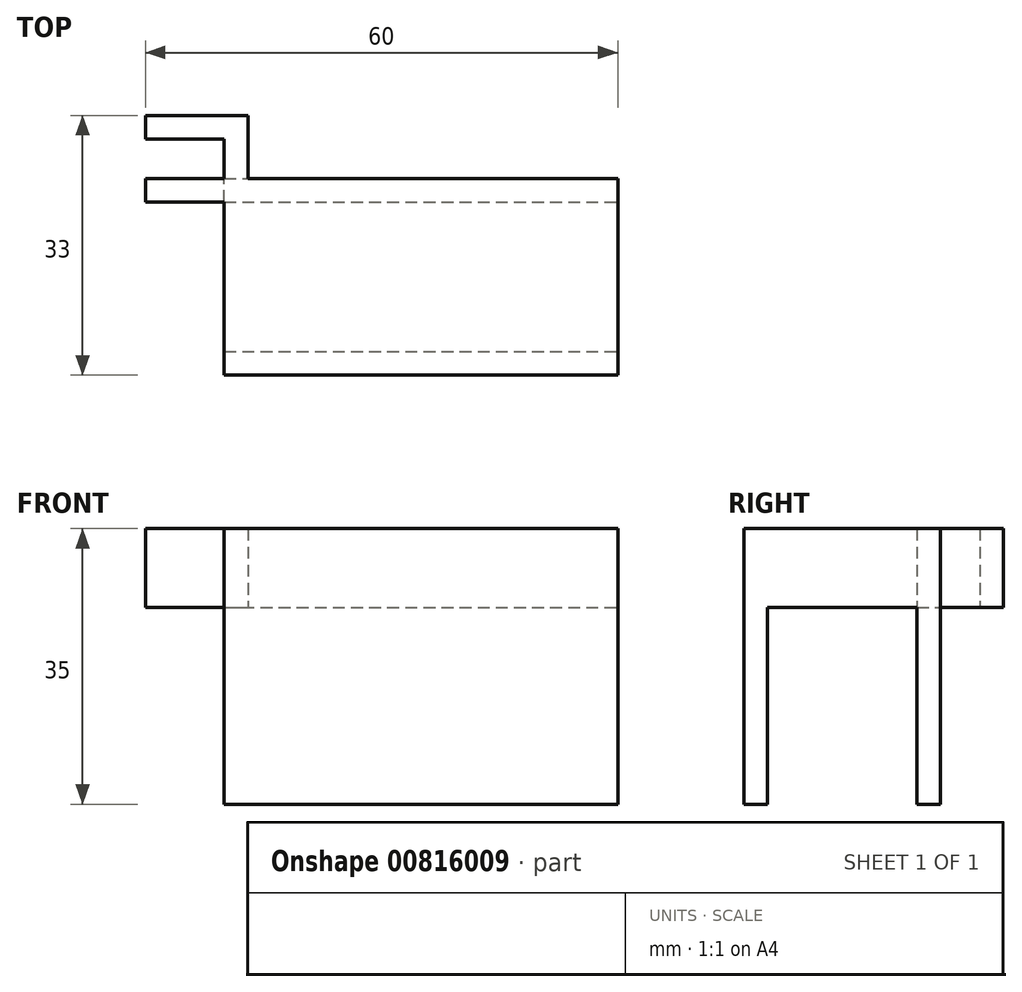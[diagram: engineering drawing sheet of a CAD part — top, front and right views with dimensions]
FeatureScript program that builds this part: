
annotation { "Feature Type Name" : "Feature", "Feature Type Description" : "" }
export const myFeature = defineFeature(function(context is Context, id is Id, definition is map)
    precondition{}
    {
        {
            var Q0;
            Q0=qCreatedBy(makeId("Top.planeOp"),FACE);
            var sketch = newSketch(context, id + "F0", { "sketchPlane" : qUnion([Q0])});
            skLineSegment(sketch, "E0", {"start": v(-32.94, 19.94) * mm, "end": v(-22.94, 19.94) * mm});
            skLineSegment(sketch, "E1", {"start": v(-22.94, 19.94) * mm, "end": v(-22.94, 14.94) * mm});
            skLineSegment(sketch, "E2", {"start": v(-22.94, 14.94) * mm, "end": v(-32.94, 14.94) * mm});
            skLineSegment(sketch, "E3.0", {"start": v(-22.94, 11.94) * mm, "end": v(-32.94, 11.94) * mm});
            skLineSegment(sketch, "E3.1", {"start": v(-19.94, 22.94) * mm, "end": v(-19.94, 14.94) * mm});
            skLineSegment(sketch, "E3.2", {"start": v(-32.94, 22.94) * mm, "end": v(-19.94, 22.94) * mm});
            skLineSegment(sketch, "E4", {"start": v(-32.94, 19.94) * mm, "end": v(-32.94, 14.94) * mm, "construction": true});
            skPoint(sketch, "E5.orphan", {"position": v(-32.94, 6.82) * mm});
            skLineSegment(sketch, "E6", {"start": v(-32.94, 22.94) * mm, "end": v(-32.94, 19.94) * mm});
            skLineSegment(sketch, "E7", {"start": v(-32.94, 11.94) * mm, "end": v(-32.94, 14.94) * mm});
            skLineSegment(sketch, "E8.left", {"start": v(-19.94, 16.37) * mm, "end": v(-19.94, 14.94) * mm});
            skLineSegment(sketch, "E9.bottom", {"start": v(-19.94, 14.94) * mm, "end": v(27.06, 14.94) * mm});
            skLineSegment(sketch, "E9.top", {"start": v(-22.94, -10.06) * mm, "end": v(27.06, -10.06) * mm});
            skLineSegment(sketch, "E9.left", {"start": v(-22.94, 11.94) * mm, "end": v(-22.94, -10.06) * mm});
            skLineSegment(sketch, "E9.right", {"start": v(27.06, 14.94) * mm, "end": v(27.06, -10.06) * mm});
            skSolve(sketch);
        }
        {
            var Q0;
            Q0 = qSketchRegion(id + "F0", true);
            extrude(context, id + "F1", {"entities" : qUnion([Q0]), "depth" : 10 * mm, "offsetDistance" : 25 * mm});
        }
        {
            var Q0;
            Q0=makeQuery(id+"F1.opExtrude","CAP_FACE",FACE,{"disambiguationData":[OSD([sQuery(id+"F0.wireOp",EDGE,"E0"),sQuery(id+"F0.wireOp",EDGE,"E1"),sQuery(id+"F0.wireOp",EDGE,"E2"),sQuery(id+"F0.wireOp",EDGE,"E3.0"),sQuery(id+"F0.wireOp",EDGE,"E3.1"),sQuery(id+"F0.wireOp",EDGE,"E3.2"),sQuery(id+"F0.wireOp",EDGE,"E6"),sQuery(id+"F0.wireOp",EDGE,"E7"),sQuery(id+"F0.wireOp",EDGE,"E8.left"),sQuery(id+"F0.wireOp",EDGE,"E9.bottom"),sQuery(id+"F0.wireOp",EDGE,"E9.top"),sQuery(id+"F0.wireOp",EDGE,"E9.left"),sQuery(id+"F0.wireOp",EDGE,"E9.right")])],"isStart":true});
            var sketch = newSketch(context, id + "F2", { "sketchPlane" : qUnion([Q0])});
            skLineSegment(sketch, "E10.bottom", {"start": v(-22.94, 7.06) * mm, "end": v(27.06, 7.06) * mm});
            skLineSegment(sketch, "E10.top", {"start": v(-22.94, -11.94) * mm, "end": v(27.06, -11.94) * mm});
            skLineSegment(sketch, "E10.left", {"start": v(-22.94, 7.06) * mm, "end": v(-22.94, -11.94) * mm});
            skLineSegment(sketch, "E10.right", {"start": v(27.06, 7.06) * mm, "end": v(27.06, -11.94) * mm});
            skLineSegment(sketch, "E11", {"start": v(-22.94, -11.94) * mm, "end": v(-22.94, -14.94) * mm});
            skLineSegment(sketch, "E12", {"start": v(-22.94, -14.94) * mm, "end": v(-19.94, -14.94) * mm});
            skSolve(sketch);
        }
        {
            var Q0;
            {var subQ1=sQuery(id+"F2.wireOp",EDGE,"E10.top");Q0=makeQuery(id+"F2.imprint","IMPRINT",FACE,{"disambiguationData":[TD([[makeQuery(id+"F2.imprint","IMPRINT",EDGE,{"derivedFrom":subQ1}),-1.0]])]});}
            var Q1;
            {var subQ0=sQuery(id+"F2.wireOp",EDGE,"E10.bottom");Q1=makeQuery(id+"F2.imprint","IMPRINT",FACE,{"disambiguationData":[TD([[makeQuery(id+"F2.imprint","IMPRINT",EDGE,{"derivedFrom":subQ0}),1.0]])]});}
            extrude(context, id + "F3", {"entities" : qUnion([Q0, Q1]), "operationType" : NewBodyOperationType.ADD, "depth" : 25 * mm, "offsetDistance" : 25 * mm});
        }
    });
